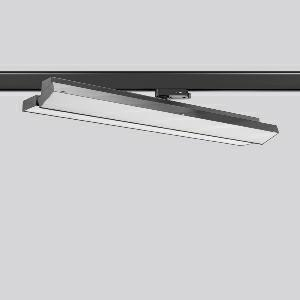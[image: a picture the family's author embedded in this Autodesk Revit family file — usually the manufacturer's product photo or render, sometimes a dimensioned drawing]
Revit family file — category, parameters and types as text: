
# Revit family: tx-move_742164_003_754e
name_source: partatom
category: Lighting Fixtures
units: mm (PartAtom-declared; Revit-internal decimal feet)

## family parameters
Cut with Voids When Loaded = No
Host = Face
Light Source = No
Part Type = Normal
Room Calculation Point = No
Round Connector Dimension = Use Diameter
Shared = No

## types (1)
- MultiLumen 1 (1 x LED Modul 830, 2450 lm, 3000)
    Apparent Load = 41 VA
    CIE Flux Codes = 47 79 96 100 100
    Color Rendering = 80
    Color Temperature = 3000
    Default Elevation = 1800 mm
    Description = Series: TX-MOVE
Multifunctional surface-mounted spotlight for area lighting. Very flat design. Housing: sheet steel, powder-coated. Rotation range: 356°. Swivel range: 90°. Consistent alignment possible with visible tilt scale. High-efficiency LED units with flush-mounted opal diffuser made of non-yellowing PMMA. Symmetrical wide beam light emission. With multi adaptor for 3-circuit tracks 230 V. Suitable for Track on ceiling. MultiLumen: Luminous flux adjustable in 3 steps. Factory setting is the highest luminous flux. Environmentally friendly and resource-saving due to replaceable and recyclable components. 
Colour: deep black, matt (RAL 9005)
Length: 570 mm
Width: 119 mm
Height: 92 mm
Lamp: LED
Socket: without socket
Colour temperature: 3000K
Colour rendering index (CRI): 80
System power: 41 W
Rated luminous flux: 4900 lm
Luminous efficiency: 120 lm/W
System power 2: 57 W
Rated luminous flux 2: 6650 lm
Luminous efficiency 2: 117 lm/W
System power 3: 73 W
Rated luminous flux 3: 8150 lm
Luminous efficiency 3: 112 lm/W
Control gear: Regulated power supply
Protection class: I
Type of protection: IP 20
    Height = 75 mm
    Lamp = 1 x LED Modul 830
    Lamp Light Flux = 2450 lm
    Lamp count = 1
    Length = 569 mm
    Lifetime = 50000 h
    Luminous efficacy = 120 lm/W
    Manufacturer = RZB
    ModVariant = No
    Model = 742164.003
    Mounting Place = Ceiling
    Mounting Type = Surface mounted
    Number of Poles = 1
    OnlyDefault = Yes
    Power Factor = 1
    Product Name = TX-MOVE
    Product group = Track mounted projectors
    ProductGroupID = 301
    Protection Class = Protection class I
    Protection Degree = IP 20
    RLX_Detail_Level = 1
    RLX_Emergency_Light_Flux = 0 lm
    RLX_Emergency_Type = 0
    RLX_Emergency_Type_DB = No
    RlxData = <blob elided: 35729 chars, md5=642ee4da>
    Socket = socket
    Standby Power = 0 W
    System Light Flux = 4900 lm
    System Power = 41 W
    Type Comments = MultiLumen 1
    Type Image = 742164.003.jpg
    URL = http://relux.com
    VarID = multilumen_1
    Voltage = 0 V
    Weight = 0.00 kg
    Width = 119 mm

## geometry (parser evidence)
native form markers: Blend x4, Sweep x15
no freeform markers — native parametric forms only
